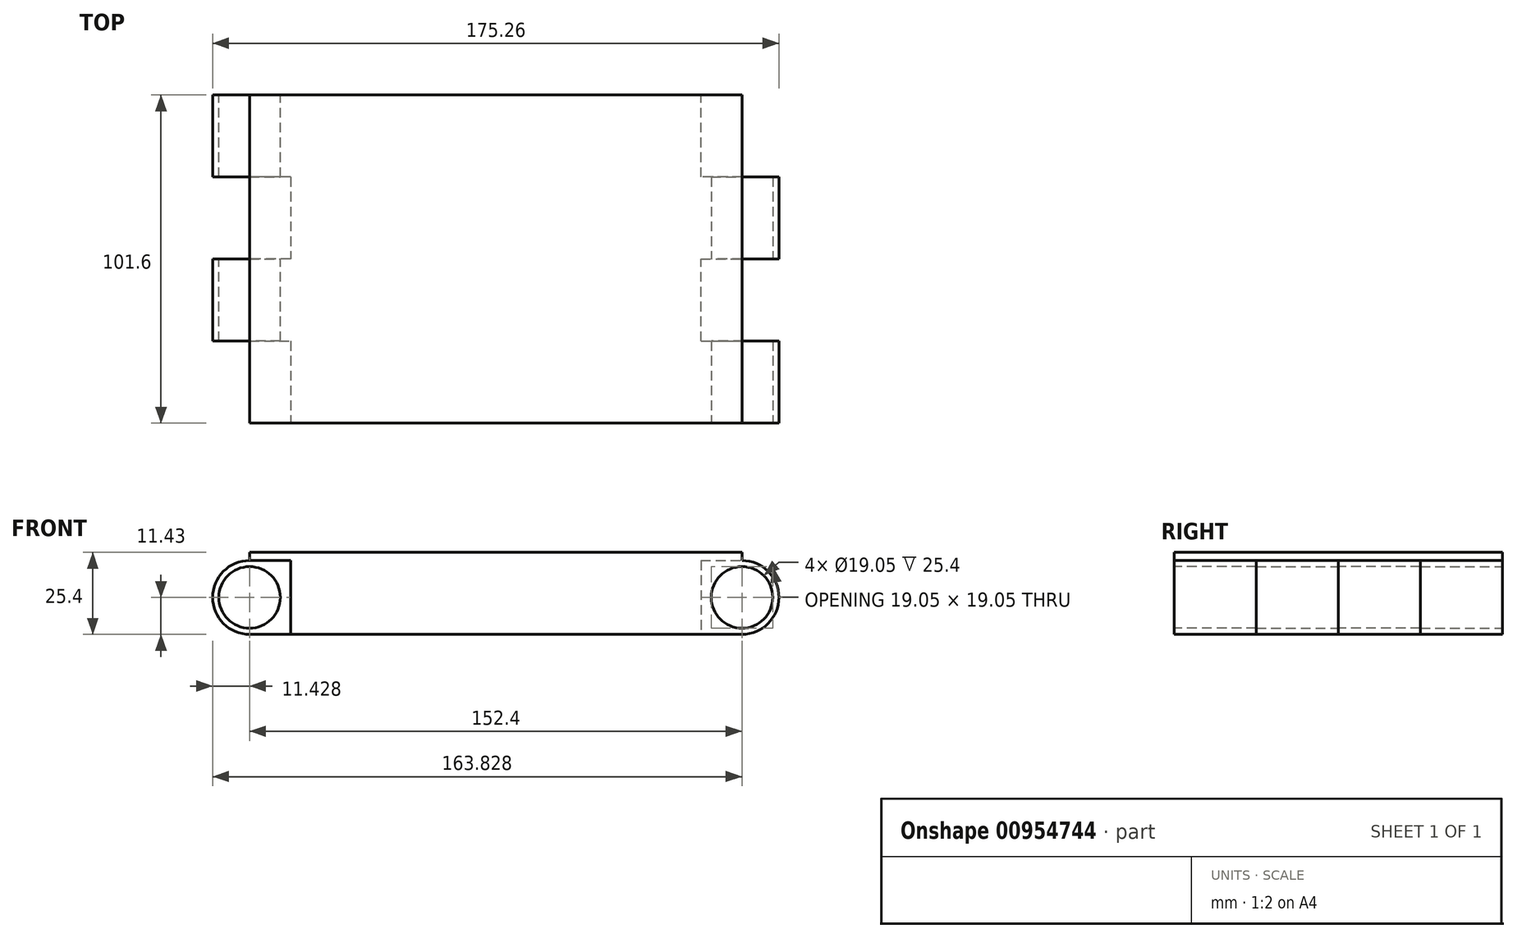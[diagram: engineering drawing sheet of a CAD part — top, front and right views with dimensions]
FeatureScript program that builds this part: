
annotation { "Feature Type Name" : "Feature", "Feature Type Description" : "" }
export const myFeature = defineFeature(function(context is Context, id is Id, definition is map)
    precondition{}
    {
        {
            var Q0;
            Q0=qCreatedBy(makeId("Top.planeOp"),FACE);
            var sketch = newSketch(context, id + "F0", { "sketchPlane" : qUnion([Q0])});
            skLineSegment(sketch, "E0", {"start": v(-137.24, 101.6) * mm, "end": v(-137.24, 76.2) * mm});
            skLineSegment(sketch, "E1", {"start": v(-137.24, 76.2) * mm, "end": v(-111.84, 76.2) * mm});
            skLineSegment(sketch, "E2", {"start": v(-111.84, 76.2) * mm, "end": v(-111.84, 50.8) * mm});
            skLineSegment(sketch, "E3", {"start": v(-111.84, 50.8) * mm, "end": v(-137.24, 50.8) * mm});
            skLineSegment(sketch, "E4", {"start": v(-137.24, 50.8) * mm, "end": v(-137.24, 25.4) * mm});
            skLineSegment(sketch, "E5", {"start": v(-137.24, 25.4) * mm, "end": v(-111.84, 25.4) * mm});
            skLineSegment(sketch, "E6", {"start": v(-111.84, 25.4) * mm, "end": v(-111.84, 0) * mm});
            skLineSegment(sketch, "E7", {"start": v(-111.84, 0) * mm, "end": v(40.56, 0) * mm});
            skLineSegment(sketch, "E8", {"start": v(40.56, 0) * mm, "end": v(40.56, 25.4) * mm});
            skLineSegment(sketch, "E9", {"start": v(40.56, 25.4) * mm, "end": v(15.16, 25.4) * mm});
            skLineSegment(sketch, "E10", {"start": v(15.16, 25.4) * mm, "end": v(15.16, 50.8) * mm});
            skLineSegment(sketch, "E11", {"start": v(15.16, 50.8) * mm, "end": v(40.56, 50.8) * mm});
            skLineSegment(sketch, "E12", {"start": v(40.56, 50.8) * mm, "end": v(40.56, 76.2) * mm});
            skLineSegment(sketch, "E13", {"start": v(40.56, 76.2) * mm, "end": v(15.16, 76.2) * mm});
            skLineSegment(sketch, "E14", {"start": v(-137.24, 101.6) * mm, "end": v(15.16, 101.6) * mm});
            skLineSegment(sketch, "E15", {"start": v(15.16, 101.6) * mm, "end": v(15.16, 76.2) * mm});
            skSolve(sketch);
        }
        {
            var Q0;
            Q0 = qSketchRegion(id + "F0", true);
            extrude(context, id + "F1", {"entities" : qUnion([Q0]), "depth" : 25.4 * mm, "offsetDistance" : 25.4 * mm});
        }
        {
            var Q0;
            Q0=makeQuery(id+"F1.opExtrude","SWEPT_FACE",FACE,{"disambiguationData":[OSD([sQuery(id+"F0.wireOp",EDGE,"E3")])]});
            var sketch = newSketch(context, id + "F2", { "sketchPlane" : qUnion([Q0])});
            skCircle(sketch, "E16", {"center": v(124.54, 11.43) * mm, "radius": 9.53 * mm});
            skCircle(sketch, "E17", {"center": v(124.54, 11.43) * mm, "radius": 11.43 * mm});
            skLineSegment(sketch, "E18.bottom", {"start": v(111.84, 25.4) * mm, "end": v(124.54, 25.4) * mm});
            skLineSegment(sketch, "E18.top", {"start": v(111.84, 22.86) * mm, "end": v(124.54, 22.86) * mm});
            skLineSegment(sketch, "E18.left", {"start": v(111.84, 25.4) * mm, "end": v(111.84, 22.86) * mm});
            skLineSegment(sketch, "E18.right", {"start": v(124.54, 25.4) * mm, "end": v(124.54, 22.86) * mm});
            skSolve(sketch);
        }
        {
            var Q0;
            {var subQ3=sQuery(id+"F2.wireOp",EDGE,"E18.right");Q0=makeQuery(id+"F2.imprint","IMPRINT",FACE,{"disambiguationData":[TD([[makeQuery(id+"F2.imprint","IMPRINT",EDGE,{"derivedFrom":subQ3}),1.0]])]});}
            extrude(context, id + "F3", {"entities" : qUnion([Q0]), "operationType" : NewBodyOperationType.REMOVE, "endBound" : BoundingType.UP_TO_NEXT, "oppositeDirection" : true, "depth" : 25.4 * mm, "offsetDistance" : 25.4 * mm, "hasSecondDirection" : true, "secondDirectionBound" : SecondDirectionBoundingType.THROUGH_ALL, "secondDirectionOppositeDirection" : false, "secondDirectionDepth" : 25.4 * mm});
        }
        {
            var Q0;
            Q0=makeQuery(id+"F2.imprint","IMPRINT",FACE,{"disambiguationData":[TD([[makeQuery(id+"F2.imprint","IMPRINT",EDGE,{"derivedFrom":sQuery(id+"F2.wireOp",EDGE,"E16")}),1.0]])]});
            extrude(context, id + "F4", {"entities" : qUnion([Q0]), "operationType" : NewBodyOperationType.REMOVE, "oppositeDirection" : true, "depth" : 25.4 * mm, "offsetDistance" : 25.4 * mm, "hasSecondDirection" : true, "secondDirectionBound" : SecondDirectionBoundingType.THROUGH_ALL, "secondDirectionOppositeDirection" : false, "secondDirectionDepth" : 25.4 * mm});
        }
        {
            var Q0;
            Q0=makeQuery(id+"F2.imprint","IMPRINT",FACE,{"disambiguationData":[TD([[makeQuery(id+"F2.imprint","IMPRINT",EDGE,{"derivedFrom":sQuery(id+"F2.wireOp",EDGE,"E18.bottom")}),-1.0]])]});
            extrude(context, id + "F5", {"entities" : qUnion([Q0]), "operationType" : NewBodyOperationType.ADD, "endBound" : BoundingType.UP_TO_NEXT, "depth" : 25.4 * mm, "offsetDistance" : 25.4 * mm, "hasSecondDirection" : true, "secondDirectionOppositeDirection" : true, "secondDirectionDepth" : 50.8 * mm});
        }
        {
            var Q0;
            Q0=makeQuery(id+"F1.opExtrude","SWEPT_FACE",FACE,{"disambiguationData":[OSD([sQuery(id+"F0.wireOp",EDGE,"E11")])]});
            var sketch = newSketch(context, id + "F6", { "sketchPlane" : qUnion([Q0])});
            skCircle(sketch, "E19", {"center": v(27.86, 11.43) * mm, "radius": 9.53 * mm});
            skCircle(sketch, "E20", {"center": v(27.86, 11.43) * mm, "radius": 11.43 * mm});
            skLineSegment(sketch, "E21.bottom", {"start": v(15.16, 25.4) * mm, "end": v(27.86, 25.4) * mm});
            skLineSegment(sketch, "E21.top", {"start": v(15.16, 22.86) * mm, "end": v(27.86, 22.86) * mm});
            skLineSegment(sketch, "E21.left", {"start": v(15.16, 25.4) * mm, "end": v(15.16, 22.86) * mm});
            skLineSegment(sketch, "E21.right", {"start": v(27.86, 25.4) * mm, "end": v(27.86, 22.86) * mm});
            skSolve(sketch);
        }
        {
            var Q0;
            {var subQ3=sQuery(id+"F6.wireOp",EDGE,"E21.right");Q0=makeQuery(id+"F6.imprint","IMPRINT",FACE,{"disambiguationData":[TD([[makeQuery(id+"F6.imprint","IMPRINT",EDGE,{"derivedFrom":subQ3}),1.0]])]});}
            extrude(context, id + "F7", {"entities" : qUnion([Q0]), "operationType" : NewBodyOperationType.REMOVE, "endBound" : BoundingType.UP_TO_NEXT, "oppositeDirection" : true, "depth" : 25.4 * mm, "offsetDistance" : 25.4 * mm, "hasSecondDirection" : true, "secondDirectionBound" : SecondDirectionBoundingType.THROUGH_ALL, "secondDirectionOppositeDirection" : false, "secondDirectionDepth" : 25.4 * mm});
        }
        {
            var Q0;
            Q0=makeQuery(id+"F6.imprint","IMPRINT",FACE,{"disambiguationData":[TD([[makeQuery(id+"F6.imprint","IMPRINT",EDGE,{"derivedFrom":sQuery(id+"F6.wireOp",EDGE,"E19")}),1.0]])]});
            extrude(context, id + "F8", {"entities" : qUnion([Q0]), "operationType" : NewBodyOperationType.REMOVE, "endBound" : BoundingType.UP_TO_NEXT, "oppositeDirection" : true, "depth" : 25.4 * mm, "offsetDistance" : 25.4 * mm, "hasSecondDirection" : true, "secondDirectionBound" : SecondDirectionBoundingType.THROUGH_ALL, "secondDirectionOppositeDirection" : false, "secondDirectionDepth" : 25.4 * mm});
        }
        {
            var Q0;
            Q0=makeQuery(id+"F6.imprint","IMPRINT",FACE,{"disambiguationData":[TD([[makeQuery(id+"F6.imprint","IMPRINT",EDGE,{"derivedFrom":sQuery(id+"F6.wireOp",EDGE,"E21.bottom")}),-1.0]])]});
            extrude(context, id + "F9", {"entities" : qUnion([Q0]), "operationType" : NewBodyOperationType.ADD, "endBound" : BoundingType.UP_TO_NEXT, "depth" : 25.4 * mm, "offsetDistance" : 25.4 * mm, "hasSecondDirection" : true, "secondDirectionOppositeDirection" : true, "secondDirectionDepth" : 50.8 * mm});
        }
    });
